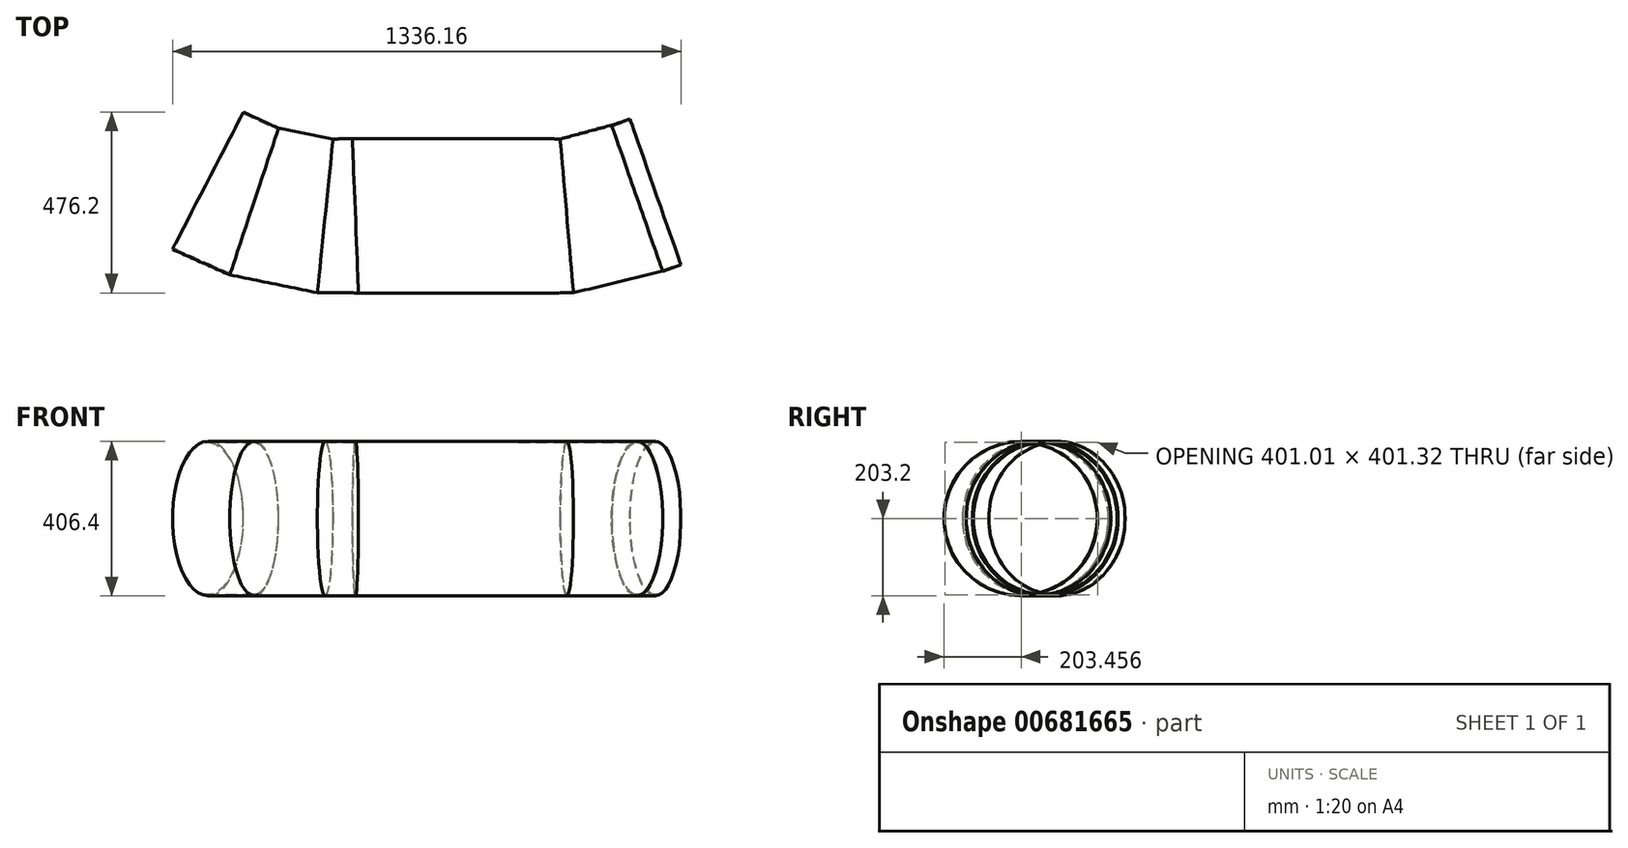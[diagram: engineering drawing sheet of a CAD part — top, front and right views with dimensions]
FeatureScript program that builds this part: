
annotation { "Feature Type Name" : "Feature", "Feature Type Description" : "" }
export const myFeature = defineFeature(function(context is Context, id is Id, definition is map)
    precondition{}
    {
        {
            var Q0;
            Q0=qCreatedBy(makeId("Top.planeOp"),FACE);
            var sketch = newSketch(context, id + "F0", { "sketchPlane" : qUnion([Q0])});
            skLineSegment(sketch, "E0", {"start": v(0, 0) * mm, "end": v(0, 203.2) * mm});
            skLineSegment(sketch, "E1", {"start": v(0, 0) * mm, "end": v(0, -203.2) * mm});
            skLineSegment(sketch, "E2", {"start": v(0, 203.2) * mm, "end": v(238.53, 203.2) * mm});
            skLineSegment(sketch, "E3", {"start": v(0, 203.2) * mm, "end": v(-205.97, 203.2) * mm});
            skLineSegment(sketch, "E4", {"start": v(0, -203.2) * mm, "end": v(222.65, -203.2) * mm});
            skLineSegment(sketch, "E5", {"start": v(0, -203.2) * mm, "end": v(-190.1, -203.2) * mm});
            skLineSegment(sketch, "E6", {"start": v(-190.1, -203.2) * mm, "end": v(-205.97, 203.2) * mm});
            skLineSegment(sketch, "E7", {"start": v(222.65, -203.2) * mm, "end": v(238.53, 203.2) * mm});
            skLineSegment(sketch, "E8", {"start": v(0, 0) * mm, "end": v(230.59, 0) * mm});
            skLineSegment(sketch, "E9", {"start": v(0, 0) * mm, "end": v(-198.04, 0) * mm});
            skLineSegment(sketch, "E10", {"start": v(222.65, -203.2) * mm, "end": v(375.05, -203.2) * mm});
            skLineSegment(sketch, "E11", {"start": v(238.53, 203.2) * mm, "end": v(340.13, 203.2) * mm});
            skLineSegment(sketch, "E12", {"start": v(340.13, 203.2) * mm, "end": v(375.05, -203.2) * mm});
            skLineSegment(sketch, "E13", {"start": v(230.59, 0) * mm, "end": v(357.59, 0) * mm});
            skLineSegment(sketch, "E14", {"start": v(357.59, 0) * mm, "end": v(542.35, 46.41) * mm});
            skLineSegment(sketch, "E15", {"start": v(375.05, -203.2) * mm, "end": v(609.31, -145.33) * mm});
            skLineSegment(sketch, "E16", {"start": v(609.31, -145.33) * mm, "end": v(475.33, 238.35) * mm});
            skLineSegment(sketch, "E17", {"start": v(475.33, 238.35) * mm, "end": v(340.13, 203.2) * mm});
            skLineSegment(sketch, "E18", {"start": v(542.35, 46.41) * mm, "end": v(590.3, 63.16) * mm});
            skLineSegment(sketch, "E19", {"start": v(475.33, 238.35) * mm, "end": v(523.3, 255.1) * mm});
            skLineSegment(sketch, "E20", {"start": v(523.3, 255.1) * mm, "end": v(590.3, 63.16) * mm});
            skLineSegment(sketch, "E21", {"start": v(609.31, -145.33) * mm, "end": v(657.27, -128.58) * mm});
            skLineSegment(sketch, "E22", {"start": v(657.27, -128.58) * mm, "end": v(590.3, 63.16) * mm});
            skLineSegment(sketch, "E23", {"start": v(-205.97, 203.2) * mm, "end": v(-256.77, 203.2) * mm});
            skLineSegment(sketch, "E24", {"start": v(-190.1, -203.2) * mm, "end": v(-298.05, -203.2) * mm});
            skLineSegment(sketch, "E25", {"start": v(-298.05, -203.2) * mm, "end": v(-256.77, 203.2) * mm});
            skLineSegment(sketch, "E26", {"start": v(-198.04, 0) * mm, "end": v(-277.41, 0) * mm});
            skLineSegment(sketch, "E27", {"start": v(-256.77, 203.2) * mm, "end": v(-400.24, 230.55) * mm});
            skLineSegment(sketch, "E28", {"start": v(-298.05, -203.2) * mm, "end": v(-528.05, -155.23) * mm});
            skLineSegment(sketch, "E29", {"start": v(-528.05, -155.23) * mm, "end": v(-400.24, 230.55) * mm});
            skLineSegment(sketch, "E30", {"start": v(-528.05, -155.23) * mm, "end": v(-678.86, -88.05) * mm});
            skLineSegment(sketch, "E31", {"start": v(-400.24, 230.55) * mm, "end": v(-492.5, 273.1) * mm});
            skLineSegment(sketch, "E32", {"start": v(-492.5, 273.1) * mm, "end": v(-678.86, -88.05) * mm});
            skLineSegment(sketch, "E33", {"start": v(-277.41, 0) * mm, "end": v(-464.14, 37.66) * mm});
            skLineSegment(sketch, "E34", {"start": v(-464.14, 37.66) * mm, "end": v(-585.68, 92.53) * mm});
            skSolve(sketch);
        }
        {
            var Q0;
            Q0=sQuery(id+"F0.wireOp",EDGE,"E16");
            cPlane(context, id + "F1", {"entities" : qUnion([Q0]), "cplaneType" : CPlaneType.LINE_ANGLE, "offset" : 25.4 * mm, "angle" : 90 * degree, "width" : 152.4 * mm, "height" : 152.4 * mm});
        }
        {
            var Q0;
            Q0=qCreatedBy(id+"F1.planeOp",FACE);
            var sketch = newSketch(context, id + "F2", { "sketchPlane" : qUnion([Q0])});
            skCircle(sketch, "E35", {"center": v(-134.49, 0) * mm, "radius": 203.2 * mm});
            skSolve(sketch);
        }
        {
            var Q0;
            Q0=sQuery(id+"F0.wireOp",EDGE,"E12");
            cPlane(context, id + "F3", {"entities" : qUnion([Q0]), "cplaneType" : CPlaneType.LINE_ANGLE, "offset" : 25.4 * mm, "angle" : 90 * degree, "width" : 152.4 * mm, "height" : 152.4 * mm});
        }
        {
            var Q0;
            Q0=qCreatedBy(id+"F3.planeOp",FACE);
            var sketch = newSketch(context, id + "F4", { "sketchPlane" : qUnion([Q0])});
            skCircle(sketch, "E36", {"center": v(-30.62, 0) * mm, "radius": 203.2 * mm});
            skSolve(sketch);
        }
        {
            var Q0;
            Q0=sQuery(id+"F0.wireOp",EDGE,"E7");
            cPlane(context, id + "F5", {"entities" : qUnion([Q0]), "cplaneType" : CPlaneType.LINE_ANGLE, "offset" : 25.4 * mm, "angle" : 90 * degree, "width" : 152.4 * mm, "height" : 152.4 * mm});
        }
        {
            var Q0;
            Q0=qCreatedBy(id+"F5.planeOp",FACE);
            var sketch = newSketch(context, id + "F6", { "sketchPlane" : qUnion([Q0])});
            skCircle(sketch, "E37", {"center": v(9, 0) * mm, "radius": 203.2 * mm});
            skSolve(sketch);
        }
        {
            var Q0;
            Q0=sQuery(id+"F0.wireOp",EDGE,"E6");
            cPlane(context, id + "F7", {"entities" : qUnion([Q0]), "cplaneType" : CPlaneType.LINE_ANGLE, "offset" : 25.4 * mm, "angle" : 90 * degree, "width" : 152.4 * mm, "height" : 152.4 * mm});
        }
        {
            var Q0;
            Q0=qCreatedBy(id+"F7.planeOp",FACE);
            var sketch = newSketch(context, id + "F8", { "sketchPlane" : qUnion([Q0])});
            skCircle(sketch, "E38", {"center": v(8.15, 0) * mm, "radius": 203.2 * mm});
            skSolve(sketch);
        }
        {
            var Q0;
            Q0=sQuery(id+"F0.wireOp",EDGE,"E25");
            cPlane(context, id + "F9", {"entities" : qUnion([Q0]), "cplaneType" : CPlaneType.LINE_ANGLE, "offset" : 25.4 * mm, "angle" : 90 * degree, "width" : 152.4 * mm, "height" : 152.4 * mm});
        }
        {
            var Q0;
            Q0=qCreatedBy(id+"F9.planeOp",FACE);
            var sketch = newSketch(context, id + "F10", { "sketchPlane" : qUnion([Q0])});
            skCircle(sketch, "E39", {"center": v(-28, 0) * mm, "radius": 203.2 * mm});
            skSolve(sketch);
        }
        {
            var Q0;
            Q0=sQuery(id+"F0.wireOp",EDGE,"E29");
            cPlane(context, id + "F11", {"entities" : qUnion([Q0]), "cplaneType" : CPlaneType.LINE_ANGLE, "offset" : 25.4 * mm, "angle" : 90 * degree, "width" : 152.4 * mm, "height" : 152.4 * mm});
        }
        {
            var Q0;
            Q0=qCreatedBy(id+"F11.planeOp",FACE);
            var sketch = newSketch(context, id + "F12", { "sketchPlane" : qUnion([Q0])});
            skCircle(sketch, "E40", {"center": v(-110.15, 0) * mm, "radius": 203.2 * mm});
            skSolve(sketch);
        }
        {
            var Q0;
            Q0=sQuery(id+"F0.wireOp",EDGE,"E32");
            cPlane(context, id + "F13", {"entities" : qUnion([Q0]), "cplaneType" : CPlaneType.LINE_ANGLE, "offset" : 25.4 * mm, "angle" : 90 * degree, "width" : 152.4 * mm, "height" : 152.4 * mm});
        }
        {
            var Q0;
            Q0=makeQuery(id+"F4.imprint","IMPRINT",FACE,{"disambiguationData":[TD([[makeQuery(id+"F4.imprint","IMPRINT",EDGE,{"derivedFrom":sQuery(id+"F4.wireOp",EDGE,"E36")}),1.0]])]});
            var Q1;
            Q1=makeQuery(id+"F2.imprint","IMPRINT",FACE,{"disambiguationData":[TD([[makeQuery(id+"F2.imprint","IMPRINT",EDGE,{"derivedFrom":sQuery(id+"F2.wireOp",EDGE,"E35")}),1.0]])]});
            loft(context, id + "F14", {"sheetProfilesArray" : [{ "sheetProfileEntities" : qUnion([Q0]) }, { "sheetProfileEntities" : qUnion([Q1]) }]});
        }
        {
            var Q1;
            Q1=makeQuery(id+"F14.opLoft","CAP_FACE",FACE,{"disambiguationData":[OSD([makeQuery(id+"F4.imprint","IMPRINT",FACE,{"disambiguationData":[TD([[makeQuery(id+"F4.imprint","IMPRINT",EDGE,{"derivedFrom":sQuery(id+"F4.wireOp",EDGE,"E36")}),1.0]])]})])],"isStart":true});
            var Q2;
            Q2=makeQuery(id+"F6.imprint","IMPRINT",FACE,{"disambiguationData":[TD([[makeQuery(id+"F6.imprint","IMPRINT",EDGE,{"derivedFrom":sQuery(id+"F6.wireOp",EDGE,"E37")}),1.0]])]});
            loft(context, id + "F15", {"operationType" : NewBodyOperationType.ADD, "sheetProfilesArray" : [{ "sheetProfileEntities" : qUnion([Q1]) }, { "sheetProfileEntities" : qUnion([Q2]) }]});
        }
        {
            var Q1;
            Q1=makeQuery(id+"F15.opLoft","CAP_FACE",FACE,{"disambiguationData":[OSD([makeQuery(id+"F6.imprint","IMPRINT",FACE,{"disambiguationData":[TD([[makeQuery(id+"F6.imprint","IMPRINT",EDGE,{"derivedFrom":sQuery(id+"F6.wireOp",EDGE,"E37")}),1.0]])]})])],"isStart":true});
            var Q2;
            Q2=makeQuery(id+"F8.imprint","IMPRINT",FACE,{"disambiguationData":[TD([[makeQuery(id+"F8.imprint","IMPRINT",EDGE,{"derivedFrom":sQuery(id+"F8.wireOp",EDGE,"E38")}),1.0]])]});
            loft(context, id + "F16", {"operationType" : NewBodyOperationType.ADD, "sheetProfilesArray" : [{ "sheetProfileEntities" : qUnion([Q1]) }, { "sheetProfileEntities" : qUnion([Q2]) }]});
        }
        {
            var Q0;
            Q0=makeQuery(id+"F16.opLoft","CAP_FACE",FACE,{"disambiguationData":[OSD([makeQuery(id+"F8.imprint","IMPRINT",FACE,{"disambiguationData":[TD([[makeQuery(id+"F8.imprint","IMPRINT",EDGE,{"derivedFrom":sQuery(id+"F8.wireOp",EDGE,"E38")}),1.0]])]})])],"isStart":true});
            var Q1;
            Q1=makeQuery(id+"F10.imprint","IMPRINT",FACE,{"disambiguationData":[TD([[makeQuery(id+"F10.imprint","IMPRINT",EDGE,{"derivedFrom":sQuery(id+"F10.wireOp",EDGE,"E39")}),1.0]])]});
            loft(context, id + "F17", {"sheetProfilesArray" : [{ "sheetProfileEntities" : qUnion([Q0]) }, { "sheetProfileEntities" : qUnion([Q1]) }]});
        }
        {
            var Q1;
            Q1=makeQuery(id+"F17.opLoft","CAP_FACE",FACE,{"disambiguationData":[OSD([makeQuery(id+"F10.imprint","IMPRINT",FACE,{"disambiguationData":[TD([[makeQuery(id+"F10.imprint","IMPRINT",EDGE,{"derivedFrom":sQuery(id+"F10.wireOp",EDGE,"E39")}),1.0]])]})])],"isStart":true});
            var Q2;
            Q2=makeQuery(id+"F12.imprint","IMPRINT",FACE,{"disambiguationData":[TD([[makeQuery(id+"F12.imprint","IMPRINT",EDGE,{"derivedFrom":sQuery(id+"F12.wireOp",EDGE,"E40")}),1.0]])]});
            loft(context, id + "F18", {"operationType" : NewBodyOperationType.ADD, "sheetProfilesArray" : [{ "sheetProfileEntities" : qUnion([Q1]) }, { "sheetProfileEntities" : qUnion([Q2]) }]});
        }
        {
            var Q0;
            Q0=qCreatedBy(id+"F13.planeOp",FACE);
            var sketch = newSketch(context, id + "F19", { "sketchPlane" : qUnion([Q0])});
            skCircle(sketch, "E41", {"center": v(-186.29, 0) * mm, "radius": 203.2 * mm});
            skSolve(sketch);
        }
        {
            var Q0;
            Q0=makeQuery(id+"F12.imprint","IMPRINT",FACE,{"disambiguationData":[TD([[makeQuery(id+"F12.imprint","IMPRINT",EDGE,{"derivedFrom":sQuery(id+"F12.wireOp",EDGE,"E40")}),1.0]])]});
            var Q1;
            Q1=makeQuery(id+"F19.imprint","IMPRINT",FACE,{"disambiguationData":[TD([[makeQuery(id+"F19.imprint","IMPRINT",EDGE,{"derivedFrom":sQuery(id+"F19.wireOp",EDGE,"E41")}),1.0]])]});
            loft(context, id + "F20", {"sheetProfilesArray" : [{ "sheetProfileEntities" : qUnion([Q0]) }, { "sheetProfileEntities" : qUnion([Q1]) }]});
        }
        {
            var Q0;
            Q0=makeQuery(id+"F20.opLoft","CAP_FACE",FACE,{"disambiguationData":[OSD([makeQuery(id+"F12.imprint","IMPRINT",FACE,{"disambiguationData":[TD([[makeQuery(id+"F12.imprint","IMPRINT",EDGE,{"derivedFrom":sQuery(id+"F12.wireOp",EDGE,"E40")}),1.0]])]})])],"isStart":true});
            var Q1;
            Q1=makeQuery(id+"F20.opLoft","CAP_FACE",FACE,{"disambiguationData":[OSD([makeQuery(id+"F19.imprint","IMPRINT",FACE,{"disambiguationData":[TD([[makeQuery(id+"F19.imprint","IMPRINT",EDGE,{"derivedFrom":sQuery(id+"F19.wireOp",EDGE,"E41")}),1.0]])]})])],"isStart":true});
            shell(context, id + "F21", {"entities" : qUnion([Q0, Q1]), "thickness" : 3.17 * mm});
        }
        {
            var Q0;
            Q0=makeQuery(id+"F17.opLoft","CAP_FACE",FACE,{"disambiguationData":[OSD([makeQuery(id+"F8.imprint","IMPRINT",FACE,{"disambiguationData":[TD([[makeQuery(id+"F8.imprint","IMPRINT",EDGE,{"derivedFrom":sQuery(id+"F8.wireOp",EDGE,"E38")}),1.0]])]})])],"isStart":true});
            var Q1;
            Q1=makeQuery(id+"F18.opLoft","CAP_FACE",FACE,{"disambiguationData":[OSD([makeQuery(id+"F12.imprint","IMPRINT",FACE,{"disambiguationData":[TD([[makeQuery(id+"F12.imprint","IMPRINT",EDGE,{"derivedFrom":sQuery(id+"F12.wireOp",EDGE,"E40")}),1.0]])]})])],"isStart":true});
            shell(context, id + "F22", {"entities" : qUnion([Q0, Q1]), "thickness" : 2.54 * mm});
        }
        {
            var Q0;
            Q0=makeQuery(id+"F14.opLoft","CAP_FACE",FACE,{"disambiguationData":[OSD([makeQuery(id+"F2.imprint","IMPRINT",FACE,{"disambiguationData":[TD([[makeQuery(id+"F2.imprint","IMPRINT",EDGE,{"derivedFrom":sQuery(id+"F2.wireOp",EDGE,"E35")}),1.0]])]})])],"isStart":true});
            var Q1;
            Q1=makeQuery(id+"F16.opLoft","CAP_FACE",FACE,{"disambiguationData":[OSD([makeQuery(id+"F8.imprint","IMPRINT",FACE,{"disambiguationData":[TD([[makeQuery(id+"F8.imprint","IMPRINT",EDGE,{"derivedFrom":sQuery(id+"F8.wireOp",EDGE,"E38")}),1.0]])]})])],"isStart":true});
            shell(context, id + "F23", {"entities" : qUnion([Q0, Q1]), "thickness" : 2.54 * mm});
        }
        {
            var Q0;
            Q0=sQuery(id+"F0.wireOp",EDGE,"E22");
            cPlane(context, id + "F24", {"entities" : qUnion([Q0]), "cplaneType" : CPlaneType.LINE_ANGLE, "offset" : 25.4 * mm, "angle" : 90 * degree, "width" : 152.4 * mm, "height" : 152.4 * mm});
        }
        {
            var Q0;
            Q0=qCreatedBy(id+"F24.planeOp",FACE);
            var sketch = newSketch(context, id + "F25", { "sketchPlane" : qUnion([Q0])});
            skCircle(sketch, "E42", {"center": v(-135.06, 0) * mm, "radius": 203.2 * mm});
            skCircle(sketch, "E43", {"center": v(-135.06, 0) * mm, "radius": 200.03 * mm});
            skSolve(sketch);
        }
        {
            var Q0;
            Q0=makeQuery(id+"F25.imprint","IMPRINT",FACE,{"disambiguationData":[TD([[makeQuery(id+"F25.imprint","IMPRINT",EDGE,{"derivedFrom":sQuery(id+"F25.wireOp",EDGE,"E42")}),1.0]])]});
            extrude(context, id + "F26", {"entities" : qUnion([Q0]), "operationType" : NewBodyOperationType.ADD, "oppositeDirection" : true, "depth" : 50.8 * mm, "offsetDistance" : 25.4 * mm});
        }
    });
